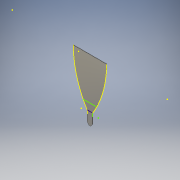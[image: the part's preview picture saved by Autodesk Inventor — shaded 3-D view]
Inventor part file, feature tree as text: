
AUTODESK INVENTOR PART (.ipt)
format: ipt  version: 2018 (Build 220112000, 112)  size: 123,392 bytes
history: native  units: in
note: dims shown in document units (in); Inventor stores cm internally (conversion verified against a paired STEP export)
features: sketch x3, extrude x1
ambient origin geometry x8: Origin, YZ Plane, XZ Plane, XY Plane, X Axis, Y Axis, Z Axis, Center Point
bodies: Solid1 (feature_tree)
feature tree (4):
  extrude  "Extrusion1"  Depth=0.4105in
  sketch  "Sketch2"  dims[d12=3.9in]
  sketch  "Sketch3"  dims[d15=0.23in d16=0.23in d17=0.028in d18=0.0in]
  sketch  "Sketch1"  dims[d10=0.4105in d11=0.5in]
